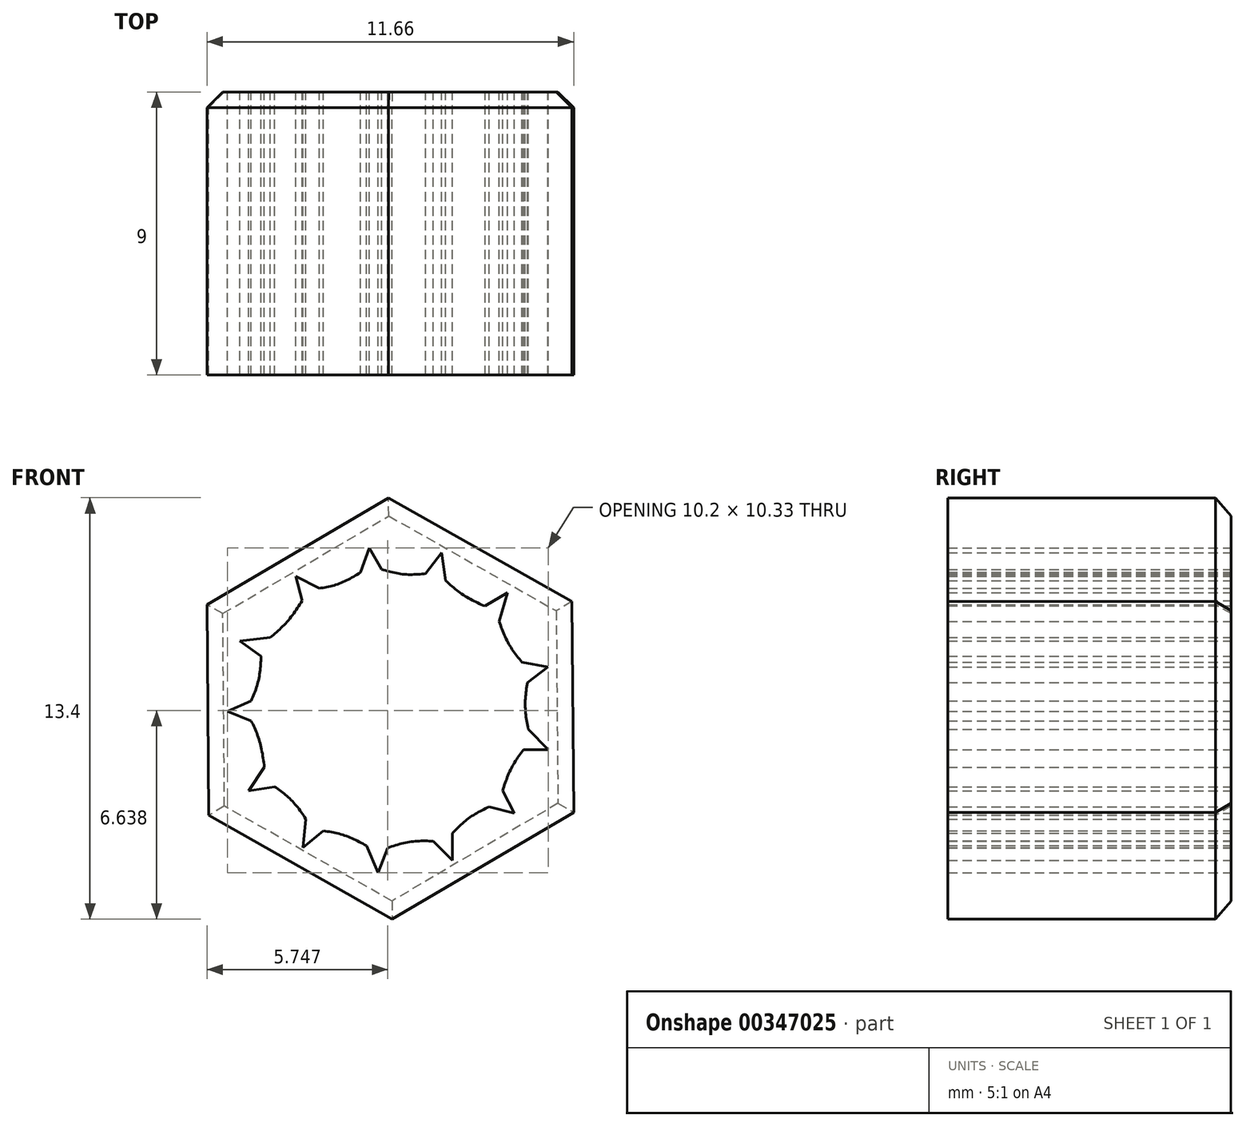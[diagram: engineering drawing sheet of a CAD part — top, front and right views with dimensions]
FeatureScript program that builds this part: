
annotation { "Feature Type Name" : "Feature", "Feature Type Description" : "" }
export const myFeature = defineFeature(function(context is Context, id is Id, definition is map)
    precondition{}
    {
        {
            var Q0;
            Q0=qCreatedBy(makeId("Front.planeOp"),FACE);
            var sketch = newSketch(context, id + "F0", { "sketchPlane" : qUnion([Q0])});
            skCircle(sketch, "E0.cCircle", {"center": v(0, 0) * mm, "radius": 5.8 * mm, "construction": true});
            skLineSegment(sketch, "E0.0", {"start": v(-0.06, 6.7) * mm, "end": v(5.77, 3.4) * mm});
            skLineSegment(sketch, "E0.1", {"start": v(5.77, 3.4) * mm, "end": v(5.83, -3.3) * mm});
            skLineSegment(sketch, "E0.2", {"start": v(5.83, -3.3) * mm, "end": v(0.06, -6.7) * mm});
            skLineSegment(sketch, "E0.3", {"start": v(0.06, -6.7) * mm, "end": v(-5.77, -3.4) * mm});
            skLineSegment(sketch, "E0.4", {"start": v(-5.77, -3.4) * mm, "end": v(-5.83, 3.3) * mm});
            skLineSegment(sketch, "E0.5", {"start": v(-5.83, 3.3) * mm, "end": v(-0.06, 6.7) * mm});
            skPoint(sketch, "E1.0.midPoint", {"position": v(-1.6, 3.98) * mm});
            skFitSpline(sketch, "E2", {"points": [v(-4.1, 2.02) * mm, v(-4.19, 0.93) * mm, v(-4.58, -0.1) * mm], "startDerivative": vector(0, -2.2) * mm, "endDerivative": vector(-0.94, -2.02) * mm});
            skFitSpline(sketch, "E3", {"points": [v(-4.1, 2.02) * mm, v(-3.27, 2.77) * mm, v(-2.59, 3.78) * mm], "startDerivative": vector(1.8, 1.43) * mm, "endDerivative": vector(1.25, 2.09) * mm});
            skFitSpline(sketch, "E4", {"points": [v(-2.59, 3.78) * mm, v(-1.6, 3.98) * mm, v(-0.63, 4.54) * mm], "startDerivative": vector(2.05, 0.24) * mm, "endDerivative": vector(1.87, 1.26) * mm});
            skFitSpline(sketch, "E5", {"points": [v(-0.63, 4.54) * mm, v(0.42, 4.27) * mm, v(1.48, 4.34) * mm], "startDerivative": vector(2.08, -0.7) * mm, "endDerivative": vector(2.13, 0.3) * mm});
            skFitSpline(sketch, "E6", {"points": [v(1.48, 4.34) * mm, v(2.36, 3.58) * mm, v(3.35, 3.13) * mm], "startDerivative": vector(1.68, -1.63) * mm, "endDerivative": vector(2.06, -0.8) * mm});
            skFitSpline(sketch, "E7", {"points": [v(3.35, 3.13) * mm, v(3.75, 2.08) * mm, v(4.42, 1.18) * mm], "startDerivative": vector(0.67, -2.17) * mm, "endDerivative": vector(1.48, -1.72) * mm});
            skFitSpline(sketch, "E8", {"points": [v(4.42, 1.18) * mm, v(4.29, 0.1) * mm, v(4.46, -1.03) * mm], "startDerivative": vector(-0.43, -2.19) * mm, "endDerivative": vector(0.5, -2.24) * mm});
            skFitSpline(sketch, "E9", {"points": [v(4.46, -1.03) * mm, v(3.84, -1.9) * mm, v(3.47, -3) * mm], "startDerivative": vector(-1.4, -1.7) * mm, "endDerivative": vector(-0.6, -2.22) * mm});
            skFitSpline(sketch, "E10", {"points": [v(3.47, -3) * mm, v(2.51, -3.47) * mm, v(1.73, -4.24) * mm], "startDerivative": vector(-2, -0.84) * mm, "endDerivative": vector(-1.47, -1.65) * mm});
            skFitSpline(sketch, "E11", {"points": [v(1.73, -4.24) * mm, v(0.64, -4.24) * mm, v(-0.44, -4.56) * mm], "startDerivative": vector(-2.2, 0.16) * mm, "endDerivative": vector(-2.14, -0.78) * mm});
            skFitSpline(sketch, "E12", {"points": [v(-0.44, -4.56) * mm, v(-1.43, -4.04) * mm, v(-2.48, -3.85) * mm], "startDerivative": vector(-1.91, 1.18) * mm, "endDerivative": vector(-2.16, 0.24) * mm});
            skFitSpline(sketch, "E13", {"points": [v(-2.48, -3.85) * mm, v(-3.15, -2.91) * mm, v(-3.95, -2.3) * mm], "startDerivative": vector(-1.2, 1.96) * mm, "endDerivative": vector(-1.76, 1.11) * mm});
            skFitSpline(sketch, "E14", {"points": [v(-3.95, -2.3) * mm, v(-4.16, -1.03) * mm, v(-4.58, -0.1) * mm], "startDerivative": vector(-0.26, 2.53) * mm, "endDerivative": vector(-1, 1.88) * mm});
            skLineSegment(sketch, "E15", {"start": v(-2.8, 3.42) * mm, "end": v(-3, 4.2) * mm});
            skLineSegment(sketch, "E16", {"start": v(-3, 4.2) * mm, "end": v(-2.26, 3.82) * mm});
            skLineSegment(sketch, "E17", {"start": v(-0.95, 4.32) * mm, "end": v(-0.67, 5.1) * mm});
            skLineSegment(sketch, "E18", {"start": v(-0.67, 5.1) * mm, "end": v(-0.28, 4.42) * mm});
            skLineSegment(sketch, "E19", {"start": v(1.12, 4.29) * mm, "end": v(1.63, 4.95) * mm});
            skLineSegment(sketch, "E20", {"start": v(1.63, 4.95) * mm, "end": v(1.76, 4.06) * mm});
            skLineSegment(sketch, "E21", {"start": v(3, 3.26) * mm, "end": v(3.72, 3.68) * mm});
            skLineSegment(sketch, "E22", {"start": v(3.72, 3.68) * mm, "end": v(3.46, 2.76) * mm});
            skLineSegment(sketch, "E23", {"start": v(4.18, 1.47) * mm, "end": v(5, 1.32) * mm});
            skLineSegment(sketch, "E24", {"start": v(5, 1.32) * mm, "end": v(4.35, 0.82) * mm});
            skLineSegment(sketch, "E25", {"start": v(4.38, -0.65) * mm, "end": v(5.02, -1.3) * mm});
            skLineSegment(sketch, "E26", {"start": v(5.02, -1.3) * mm, "end": v(4.23, -1.3) * mm});
            skLineSegment(sketch, "E27", {"start": v(3.57, -2.62) * mm, "end": v(3.94, -3.33) * mm});
            skLineSegment(sketch, "E28", {"start": v(3.94, -3.33) * mm, "end": v(3.13, -3.13) * mm});
            skLineSegment(sketch, "E29", {"start": v(1.98, -3.96) * mm, "end": v(1.98, -4.83) * mm});
            skLineSegment(sketch, "E30", {"start": v(1.98, -4.83) * mm, "end": v(1.37, -4.21) * mm});
            skLineSegment(sketch, "E31", {"start": v(-0.08, -4.43) * mm, "end": v(-0.38, -5.23) * mm});
            skLineSegment(sketch, "E32", {"start": v(-0.38, -5.23) * mm, "end": v(-0.77, -4.36) * mm});
            skLineSegment(sketch, "E33", {"start": v(-2.12, -3.89) * mm, "end": v(-2.78, -4.43) * mm});
            skLineSegment(sketch, "E34", {"start": v(-2.78, -4.43) * mm, "end": v(-2.69, -3.51) * mm});
            skLineSegment(sketch, "E35", {"start": v(-3.67, -2.49) * mm, "end": v(-4.5, -2.62) * mm});
            skLineSegment(sketch, "E36", {"start": v(-4.5, -2.62) * mm, "end": v(-4, -1.86) * mm});
            skLineSegment(sketch, "E37", {"start": v(-4.42, -0.4) * mm, "end": v(-5.18, -0.1) * mm});
            skLineSegment(sketch, "E38", {"start": v(-5.18, -0.1) * mm, "end": v(-4.42, 0.24) * mm});
            skLineSegment(sketch, "E39", {"start": v(-4.11, 1.65) * mm, "end": v(-4.78, 2.15) * mm});
            skLineSegment(sketch, "E40", {"start": v(-4.78, 2.15) * mm, "end": v(-3.82, 2.25) * mm});
            skSolve(sketch);
        }
        {
            var Q0;
            Q0=makeQuery(id+"F0.imprint","IMPRINT",FACE,{"disambiguationData":[TD([[makeQuery(id+"F0.imprint","IMPRINT",EDGE,{"derivedFrom":sQuery(id+"F0.wireOp",EDGE,"E0.0")}),-1.0]])]});
            extrude(context, id + "F1", {"entities" : qUnion([Q0]), "depth" : 9 * mm});
        }
        {
            var Q0;
            Q0=makeQuery(id+"F1.opExtrude","CAP_EDGE",EDGE,{"disambiguationData":[OSD([sQuery(id+"F0.wireOp",EDGE,"E0.5")])],"isStart":true});
            var Q1;
            Q1=makeQuery(id+"F1.opExtrude","CAP_EDGE",EDGE,{"disambiguationData":[OSD([sQuery(id+"F0.wireOp",EDGE,"E0.4")])],"isStart":true});
            var Q2;
            Q2=makeQuery(id+"F1.opExtrude","CAP_EDGE",EDGE,{"disambiguationData":[OSD([sQuery(id+"F0.wireOp",EDGE,"E0.3")])],"isStart":true});
            var Q3;
            Q3=makeQuery(id+"F1.opExtrude","CAP_EDGE",EDGE,{"disambiguationData":[OSD([sQuery(id+"F0.wireOp",EDGE,"E0.2")])],"isStart":true});
            var Q4;
            Q4=makeQuery(id+"F1.opExtrude","CAP_EDGE",EDGE,{"disambiguationData":[OSD([sQuery(id+"F0.wireOp",EDGE,"E0.1")])],"isStart":true});
            var Q5;
            Q5=makeQuery(id+"F1.opExtrude","CAP_EDGE",EDGE,{"disambiguationData":[OSD([sQuery(id+"F0.wireOp",EDGE,"E0.0")])],"isStart":true});
            chamfer(context, id + "F2", {"entities" : qUnion([Q0, Q1, Q2, Q3, Q4, Q5]), "width" : .5 * mm, "tangentPropagation" : true});
        }
    });
